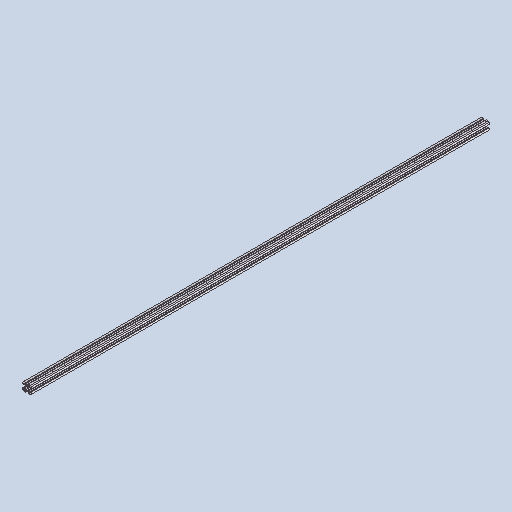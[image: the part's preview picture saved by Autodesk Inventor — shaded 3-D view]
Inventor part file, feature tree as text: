
AUTODESK INVENTOR PART (.ipt)
format: ipt  version: 2025 (Build 290162010, 162A)  size: 240,640 bytes
history: native  units: mm
features: thread x2, chamfer x2, other x1
ambient origin geometry x8: Origin, YZ Plane, XZ Plane, XY Plane, X Axis, Y Axis, Z Axis, Center Point
bodies: Volumenkörper1 (feature_tree)
feature tree (5):
  thread  "Gewinde1"  [1 undecoded]
  chamfer  "Fasen1"  Distance=2.0mm Angle=45.0deg
  thread  "Gewinde2"  [1 undecoded]
  chamfer  "Fasen2"  Distance=2.0mm Angle=45.0deg
  other  "item_37003_profil-5-20x20-natur-370_1096_high_1_1:1"
note: 2 required parameter values undecoded (feature->parameter linkage not recoverable at this tier; creation-order binding heuristic only, values carry confidence <= 0.55)
